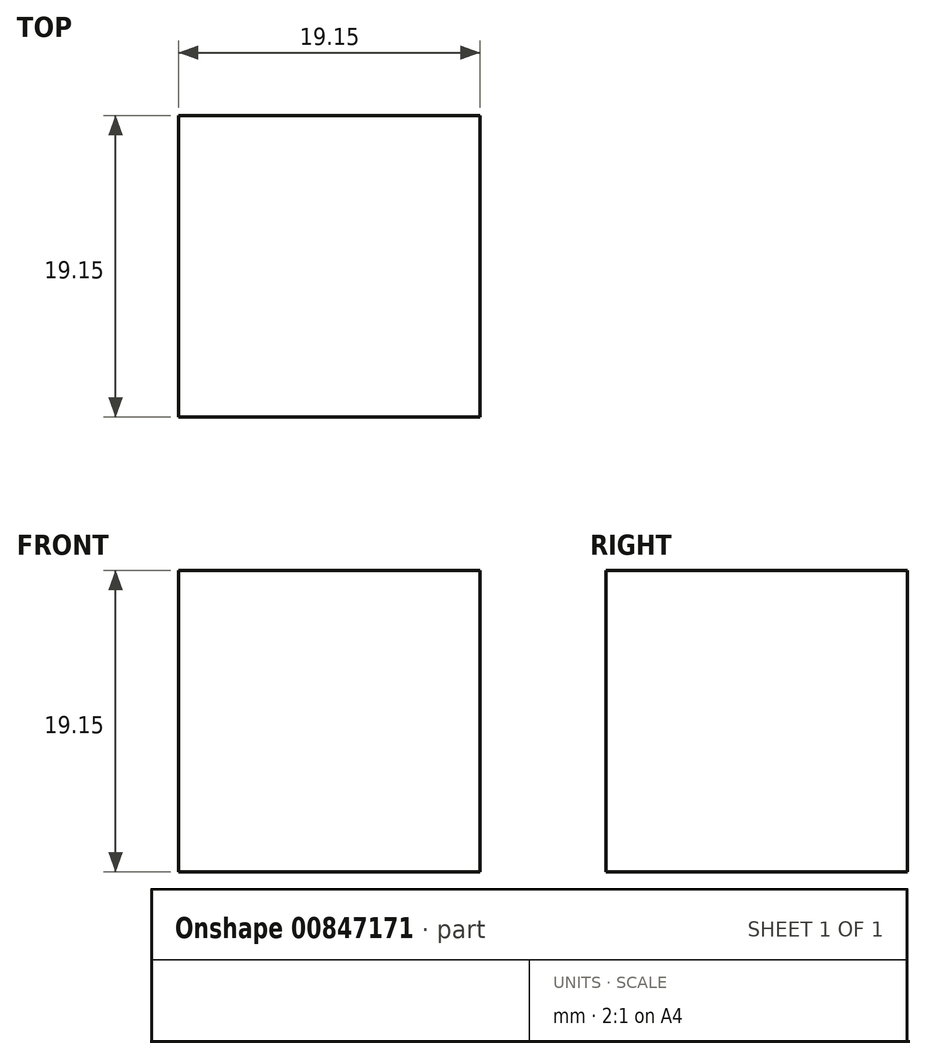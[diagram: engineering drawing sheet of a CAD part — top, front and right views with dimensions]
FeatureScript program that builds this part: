
annotation { "Feature Type Name" : "Feature", "Feature Type Description" : "" }
export const myFeature = defineFeature(function(context is Context, id is Id, definition is map)
    precondition{}
    {
        {
            var Q0;
            Q0=qCreatedBy(makeId("Front.planeOp"),FACE);
            var sketch = newSketch(context, id + "F0", { "sketchPlane" : qUnion([Q0])});
            skLineSegment(sketch, "E0.bottom", {"start": v(-36.52, 35.16) * mm, "end": v(-17.37, 35.16) * mm});
            skLineSegment(sketch, "E0.top", {"start": v(-36.52, 16.01) * mm, "end": v(-17.37, 16.01) * mm});
            skLineSegment(sketch, "E0.left", {"start": v(-36.52, 35.16) * mm, "end": v(-36.52, 16.01) * mm});
            skLineSegment(sketch, "E0.right", {"start": v(-17.37, 35.16) * mm, "end": v(-17.37, 16.01) * mm});
            skSolve(sketch);
        }
        {
            var Q0;
            Q0=makeQuery(id+"F0.imprint","IMPRINT",FACE,{"disambiguationData":[TD([[makeQuery(id+"F0.imprint","IMPRINT",EDGE,{"derivedFrom":sQuery(id+"F0.wireOp",EDGE,"E0.bottom")}),-1.0]])]});
            extrude(context, id + "F1", {"entities" : qUnion([Q0]), "depth" : 19.15 * mm, "offsetDistance" : 25.4 * mm});
        }
    });
